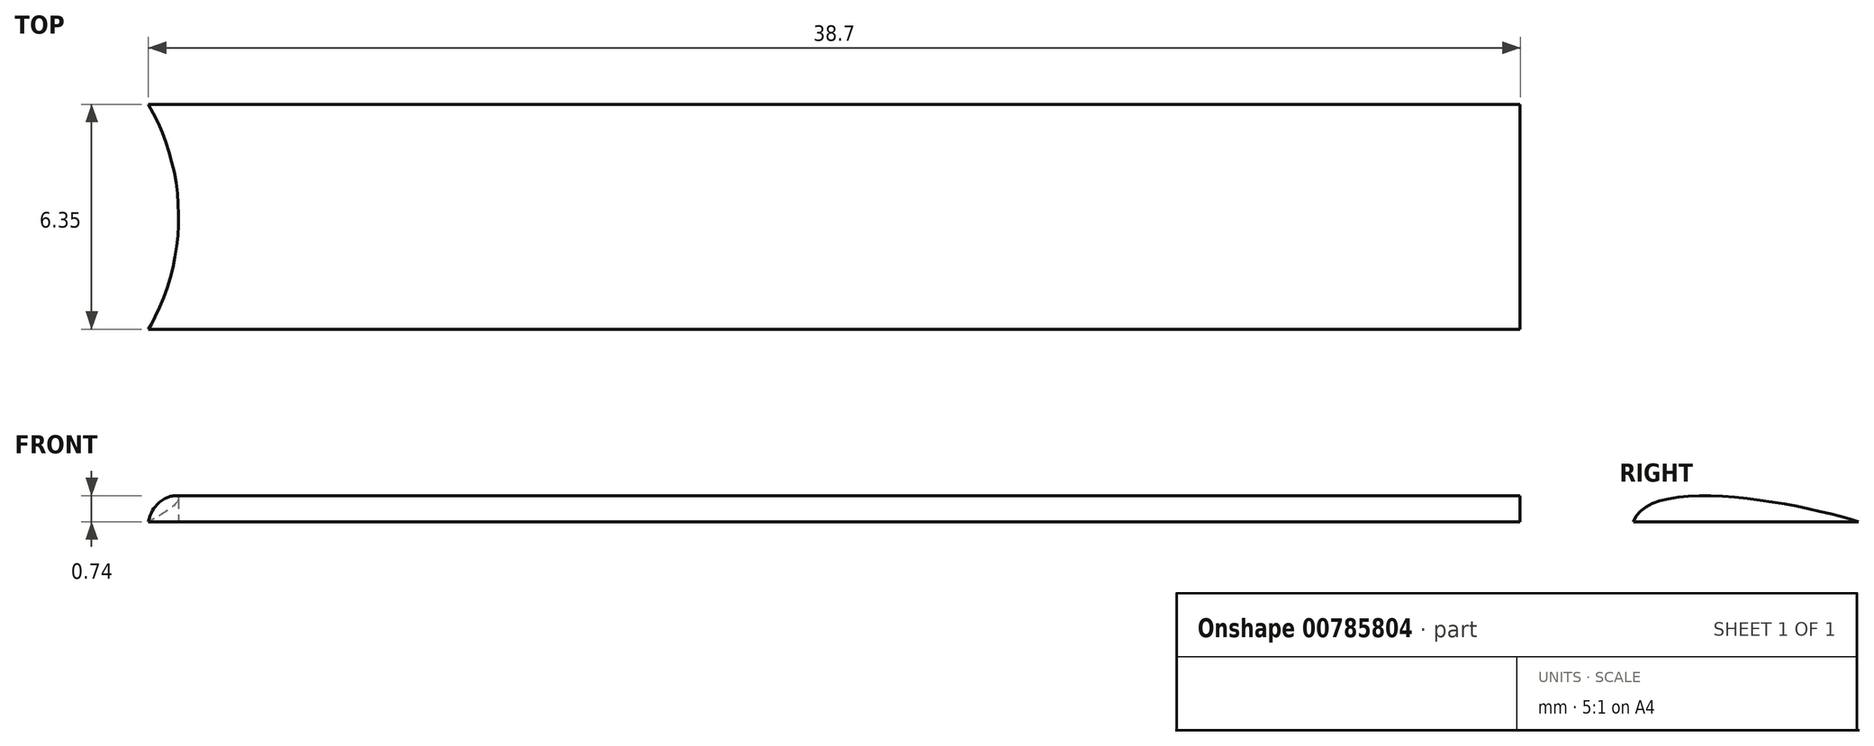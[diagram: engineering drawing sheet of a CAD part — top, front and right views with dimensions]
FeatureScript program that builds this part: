
annotation { "Feature Type Name" : "Feature", "Feature Type Description" : "" }
export const myFeature = defineFeature(function(context is Context, id is Id, definition is map)
    precondition{}
    {
        {
            var Q0;
            Q0=qCreatedBy(makeId("Right.planeOp"),FACE);
            var sketch = newSketch(context, id + "F0", { "sketchPlane" : qUnion([Q0])});
            skLineSegment(sketch, "E0", {"start": v(2.44, 0) * mm, "end": v(-3.91, 0) * mm});
            skFitSpline(sketch, "E1", {"points": [v(-3.91, 0) * mm, v(2.44, 0) * mm], "startDerivative": vector(1.26, 4) * mm, "endDerivative": vector(5.2, -1.67) * mm});
            skSolve(sketch);
        }
        {
            var Q0;
            Q0=makeQuery(id+"F0.imprint","IMPRINT",FACE,{"disambiguationData":[TD([[makeQuery(id+"F0.imprint","IMPRINT",EDGE,{"derivedFrom":sQuery(id+"F0.wireOp",EDGE,"E0")}),-1.0]])]});
            extrude(context, id + "F1", {"entities" : qUnion([Q0]), "depth" : 39.12 * mm, "offsetDistance" : 25.4 * mm});
        }
        {
            var Q0;
            Q0=makeQuery(id+"F1.opExtrude","SWEPT_FACE",FACE,{"disambiguationData":[OSD([sQuery(id+"F0.wireOp",EDGE,"E0")])]});
            var sketch = newSketch(context, id + "F2", { "sketchPlane" : qUnion([Q0])});
            skLineSegment(sketch, "E2", {"start": v(0, 0.74) * mm, "end": v(-5.08, 0.74) * mm});
            skCircle(sketch, "E3", {"center": v(-5.08, 0.74) * mm, "radius": 6.35 * mm});
            skSolve(sketch);
        }
        {
            var Q0;
            {var subQ0=sQuery(id+"F0.wireOp",EDGE,"E0");var subQ1=makeQuery(id+"F1.opExtrude","CAP_EDGE",EDGE,{"disambiguationData":[OSD([subQ0])],"isStart":true});var subQ5=makeQuery(id+"F2.imprint","IMPRINT",VERTEX,{"derivedFrom":subQ1});Q0=makeQuery(id+"F2.imprint","IMPRINT",FACE,{"disambiguationData":[TD([[makeQuery(id+"F2.imprint","IMPRINT",EDGE,{"disambiguationData":[TD([[subQ5,1.0]])],"derivedFrom":subQ1}),1.0]])]});}
            var Q1;
            {var subQ0=sQuery(id+"F0.wireOp",EDGE,"E0");var subQ1=makeQuery(id+"F1.opExtrude","CAP_EDGE",EDGE,{"disambiguationData":[OSD([subQ0])],"isStart":true});var subQ5=makeQuery(id+"F2.imprint","IMPRINT",VERTEX,{"derivedFrom":subQ1});Q1=makeQuery(id+"F2.imprint","IMPRINT",FACE,{"disambiguationData":[TD([[makeQuery(id+"F2.imprint","IMPRINT",EDGE,{"disambiguationData":[TD([[subQ5,1.0]])],"derivedFrom":subQ1}),-1.0]])]});}
            extrude(context, id + "F3", {"entities" : qUnion([Q0, Q1]), "operationType" : NewBodyOperationType.REMOVE, "oppositeDirection" : true, "depth" : 7.62 * mm, "offsetDistance" : 25.4 * mm});
        }
    });
